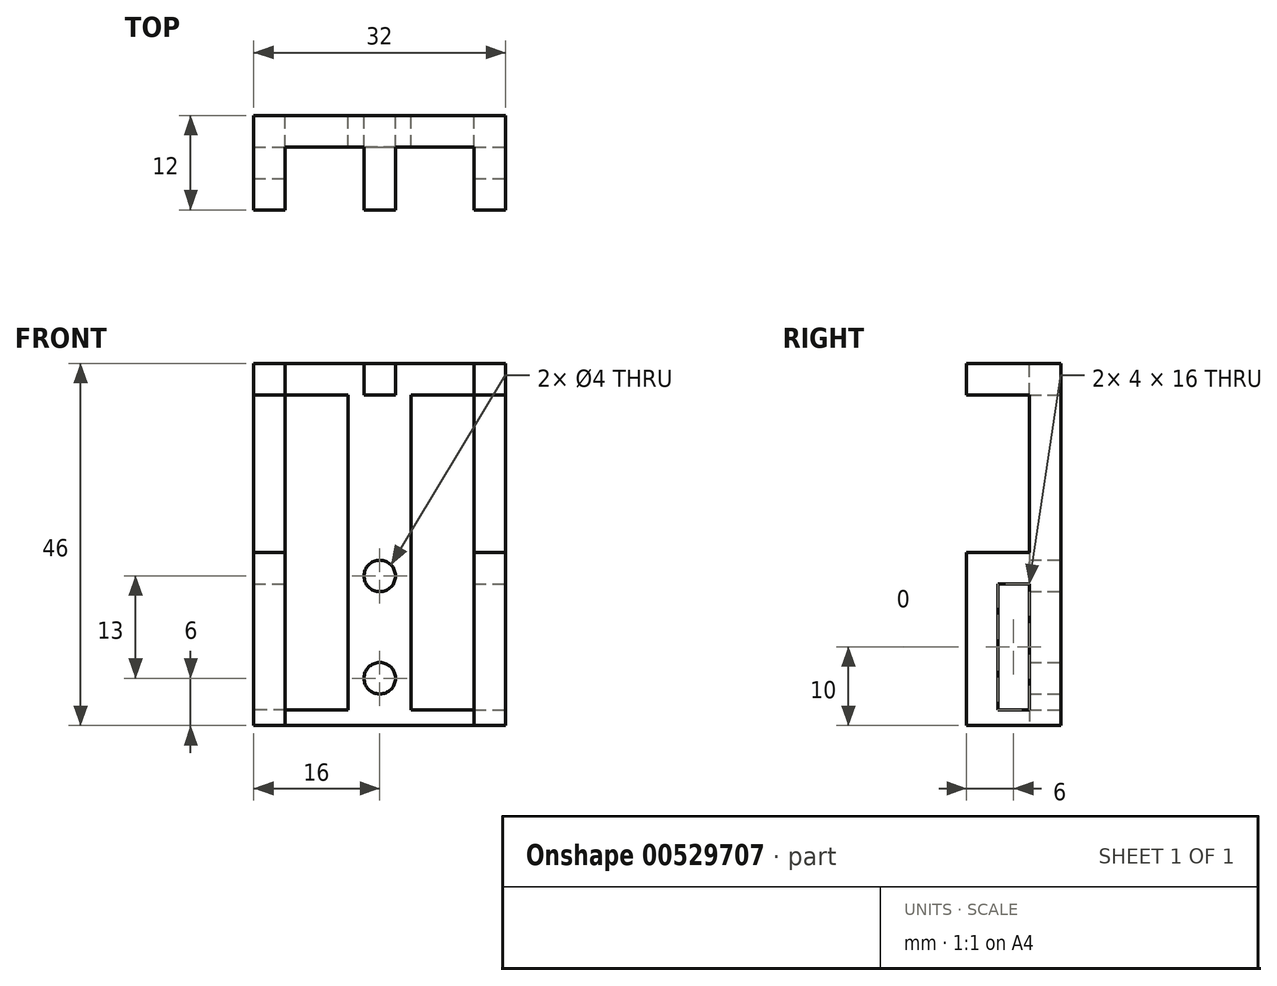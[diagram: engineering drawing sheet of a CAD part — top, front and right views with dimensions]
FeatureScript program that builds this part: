
annotation { "Feature Type Name" : "Feature", "Feature Type Description" : "" }
export const myFeature = defineFeature(function(context is Context, id is Id, definition is map)
    precondition{}
    {
        {
            var Q0;
            Q0=qCreatedBy(makeId("Front.planeOp"),FACE);
            var sketch = newSketch(context, id + "F0", { "sketchPlane" : qUnion([Q0])});
            skLineSegment(sketch, "E0.bottom", {"start": v(-16, 0) * mm, "end": v(16, 0) * mm});
            skLineSegment(sketch, "E0.top", {"start": v(-16, -46) * mm, "end": v(16, -46) * mm});
            skLineSegment(sketch, "E0.left", {"start": v(-16, -46) * mm, "end": v(-16, 0) * mm});
            skLineSegment(sketch, "E0.right", {"start": v(16, -46) * mm, "end": v(16, 0) * mm});
            skLineSegment(sketch, "E1.bottom", {"start": v(4, -4) * mm, "end": v(12, -4) * mm});
            skLineSegment(sketch, "E1.top", {"start": v(4, -44) * mm, "end": v(12, -44) * mm});
            skLineSegment(sketch, "E1.left", {"start": v(4, -4) * mm, "end": v(4, -44) * mm});
            skLineSegment(sketch, "E1.right", {"start": v(12, -4) * mm, "end": v(12, -44) * mm});
            skCircle(sketch, "E2", {"center": v(0, -27) * mm, "radius": 2 * mm});
            skLineSegment(sketch, "E3.MirrorCS", {"start": v(-4, -4) * mm, "end": v(-12, -4) * mm});
            skLineSegment(sketch, "E4.MirrorCS", {"start": v(-4, -44) * mm, "end": v(-12, -44) * mm});
            skLineSegment(sketch, "E5.MirrorCS", {"start": v(-12, -4) * mm, "end": v(-12, -44) * mm});
            skLineSegment(sketch, "E6.MirrorCS", {"start": v(-4, -4) * mm, "end": v(-4, -44) * mm});
            skCircle(sketch, "E7", {"center": v(0, -40) * mm, "radius": 2 * mm});
            skSolve(sketch);
        }
        {
            var Q0;
            Q0=qSketchRegion(id+"F0",true);
            extrude(context, id + "F1", {"entities" : qUnion([Q0]), "depth" : 4 * mm, "offsetDistance" : 25 * mm});
        }
        {
            var Q0;
            Q0=makeQuery(id+"F1.opExtrude","CAP_FACE",FACE,{"disambiguationData":[OSD([sQuery(id+"F0.wireOp",EDGE,"E0.bottom"),sQuery(id+"F0.wireOp",EDGE,"E0.top"),sQuery(id+"F0.wireOp",EDGE,"E0.left"),sQuery(id+"F0.wireOp",EDGE,"E0.right"),sQuery(id+"F0.wireOp",EDGE,"E1.bottom"),sQuery(id+"F0.wireOp",EDGE,"E1.top"),sQuery(id+"F0.wireOp",EDGE,"E1.left"),sQuery(id+"F0.wireOp",EDGE,"E1.right"),sQuery(id+"F0.wireOp",EDGE,"E2"),sQuery(id+"F0.wireOp",EDGE,"E3.MirrorCS"),sQuery(id+"F0.wireOp",EDGE,"E4.MirrorCS"),sQuery(id+"F0.wireOp",EDGE,"E5.MirrorCS"),sQuery(id+"F0.wireOp",EDGE,"E6.MirrorCS"),sQuery(id+"F0.wireOp",EDGE,"E7")])],"isStart":false});
            var sketch = newSketch(context, id + "F2", { "sketchPlane" : qUnion([Q0])});
            skLineSegment(sketch, "E8.bottom", {"start": v(-16, 0) * mm, "end": v(-12, 0) * mm});
            skLineSegment(sketch, "E8.top", {"start": v(-16, -4) * mm, "end": v(-12, -4) * mm});
            skLineSegment(sketch, "E8.left", {"start": v(-16, 0) * mm, "end": v(-16, -4) * mm});
            skLineSegment(sketch, "E8.right", {"start": v(-12, 0) * mm, "end": v(-12, -4) * mm});
            skLineSegment(sketch, "E9.bottom", {"start": v(12, -4) * mm, "end": v(16, -4) * mm});
            skLineSegment(sketch, "E9.top", {"start": v(12, 0) * mm, "end": v(16, 0) * mm});
            skLineSegment(sketch, "E9.left", {"start": v(12, -4) * mm, "end": v(12, 0) * mm});
            skLineSegment(sketch, "E9.right", {"start": v(16, -4) * mm, "end": v(16, 0) * mm});
            skLineSegment(sketch, "E10.bottom", {"start": v(-2, 0) * mm, "end": v(2, 0) * mm});
            skLineSegment(sketch, "E10.top", {"start": v(-2, -4) * mm, "end": v(2, -4) * mm});
            skLineSegment(sketch, "E10.left", {"start": v(-2, 0) * mm, "end": v(-2, -4) * mm});
            skLineSegment(sketch, "E10.right", {"start": v(2, 0) * mm, "end": v(2, -4) * mm});
            skLineSegment(sketch, "E11.bottom", {"start": v(-16, -24) * mm, "end": v(-12, -24) * mm});
            skLineSegment(sketch, "E11.top", {"start": v(-16, -28) * mm, "end": v(-12, -28) * mm});
            skLineSegment(sketch, "E11.left", {"start": v(-16, -24) * mm, "end": v(-16, -28) * mm});
            skLineSegment(sketch, "E11.right", {"start": v(-12, -24) * mm, "end": v(-12, -28) * mm});
            skLineSegment(sketch, "E12.bottom", {"start": v(12, -24) * mm, "end": v(16, -24) * mm});
            skLineSegment(sketch, "E12.top", {"start": v(12, -28) * mm, "end": v(16, -28) * mm});
            skLineSegment(sketch, "E12.left", {"start": v(12, -24) * mm, "end": v(12, -28) * mm});
            skLineSegment(sketch, "E12.right", {"start": v(16, -24) * mm, "end": v(16, -28) * mm});
            skLineSegment(sketch, "E13.bottom", {"start": v(-12, -44) * mm, "end": v(-16, -44) * mm});
            skLineSegment(sketch, "E13.top", {"start": v(-12, -46) * mm, "end": v(-16, -46) * mm});
            skLineSegment(sketch, "E13.left", {"start": v(-12, -44) * mm, "end": v(-12, -46) * mm});
            skLineSegment(sketch, "E13.right", {"start": v(-16, -44) * mm, "end": v(-16, -46) * mm});
            skLineSegment(sketch, "E14.bottom", {"start": v(12, -44) * mm, "end": v(16, -44) * mm});
            skLineSegment(sketch, "E14.top", {"start": v(12, -46) * mm, "end": v(16, -46) * mm});
            skLineSegment(sketch, "E14.left", {"start": v(12, -44) * mm, "end": v(12, -46) * mm});
            skLineSegment(sketch, "E14.right", {"start": v(16, -44) * mm, "end": v(16, -46) * mm});
            skSolve(sketch);
        }
        {
            var Q0;
            Q0 = qSketchRegion(id + "F2", true);
            extrude(context, id + "F3", {"entities" : qUnion([Q0]), "operationType" : NewBodyOperationType.ADD, "depth" : 8 * mm, "offsetDistance" : 25 * mm});
        }
        {
            var Q0;
            Q0=makeQuery(id+"F3.opExtrude","CAP_FACE",FACE,{"disambiguationData":[OSD([sQuery(id+"F2.wireOp",EDGE,"E8.bottom"),sQuery(id+"F2.wireOp",EDGE,"E8.top"),sQuery(id+"F2.wireOp",EDGE,"E8.left"),sQuery(id+"F2.wireOp",EDGE,"E8.right")])],"isStart":false});
            var sketch = newSketch(context, id + "F4", { "sketchPlane" : qUnion([Q0])});
            skLineSegment(sketch, "E15.bottom", {"start": v(-12, -24) * mm, "end": v(-16, -24) * mm});
            skLineSegment(sketch, "E15.top", {"start": v(-12, -46) * mm, "end": v(-16, -46) * mm});
            skLineSegment(sketch, "E15.left", {"start": v(-12, -24) * mm, "end": v(-12, -46) * mm});
            skLineSegment(sketch, "E15.right", {"start": v(-16, -24) * mm, "end": v(-16, -46) * mm});
            skLineSegment(sketch, "E16.bottom", {"start": v(12, -24) * mm, "end": v(16, -24) * mm});
            skLineSegment(sketch, "E16.top", {"start": v(12, -46) * mm, "end": v(16, -46) * mm});
            skLineSegment(sketch, "E16.left", {"start": v(12, -24) * mm, "end": v(12, -46) * mm});
            skLineSegment(sketch, "E16.right", {"start": v(16, -24) * mm, "end": v(16, -46) * mm});
            skSolve(sketch);
        }
        {
            var Q0;
            Q0 = qSketchRegion(id + "F4", true);
            extrude(context, id + "F5", {"entities" : qUnion([Q0]), "operationType" : NewBodyOperationType.ADD, "oppositeDirection" : true, "depth" : 4 * mm, "offsetDistance" : 25 * mm});
        }
    });
